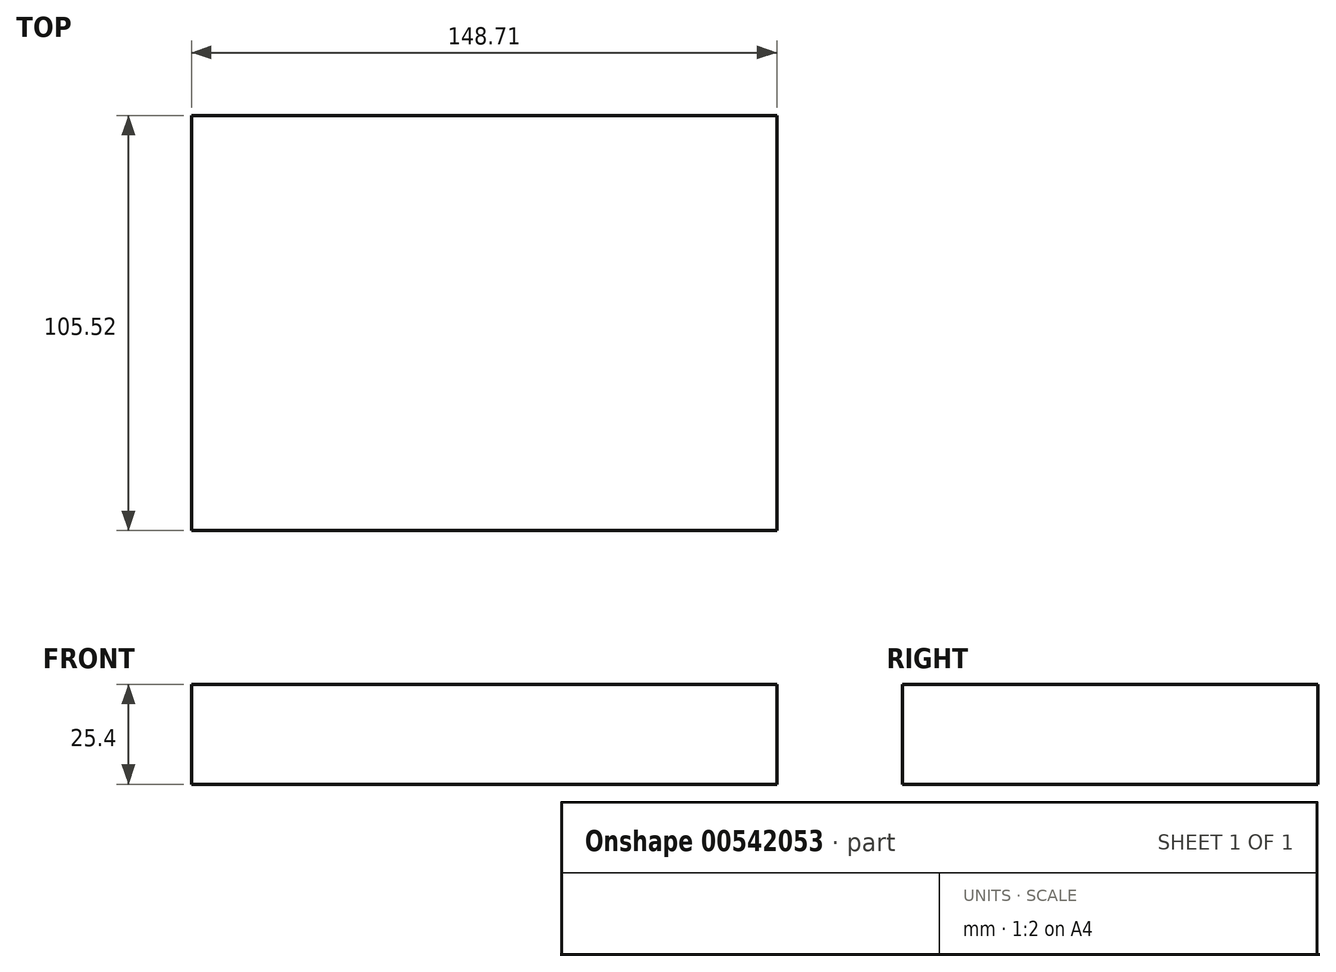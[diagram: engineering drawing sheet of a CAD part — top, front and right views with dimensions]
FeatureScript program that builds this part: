
annotation { "Feature Type Name" : "Feature", "Feature Type Description" : "" }
export const myFeature = defineFeature(function(context is Context, id is Id, definition is map)
    precondition{}
    {
        {
            var Q0;
            Q0=qCreatedBy(makeId("Top.planeOp"),FACE);
            var sketch = newSketch(context, id + "F0", { "sketchPlane" : qUnion([Q0])});
            skLineSegment(sketch, "E0.bottom", {"start": v(-124.37, 49.68) * mm, "end": v(24.34, 49.68) * mm});
            skLineSegment(sketch, "E0.top", {"start": v(-124.37, -55.84) * mm, "end": v(24.34, -55.84) * mm});
            skLineSegment(sketch, "E0.left", {"start": v(-124.37, 49.68) * mm, "end": v(-124.37, -55.84) * mm});
            skLineSegment(sketch, "E0.right", {"start": v(24.34, 49.68) * mm, "end": v(24.34, -55.84) * mm});
            skSolve(sketch);
        }
        {
            var Q0;
            Q0=makeQuery(id+"F0.imprint","IMPRINT",FACE,{"disambiguationData":[TD([[makeQuery(id+"F0.imprint","IMPRINT",EDGE,{"derivedFrom":sQuery(id+"F0.wireOp",EDGE,"E0.bottom")}),-1.0]])]});
            extrude(context, id + "F1", {"entities" : qUnion([Q0]), "depth" : 25.4 * mm, "offsetDistance" : 25.4 * mm});
        }
    });
